# Revit family: xxSink-Single_Bowl-American_Standard-PEKOE-18SB.9332200A.075
name_source: partatom
category: Plumbing Fixtures
revit_build: Autodesk Revit 2014 (Build: 20130308_1515(x64)
units: mm (PartAtom-declared; Revit-internal decimal feet)

## types (1)
- 18SB.9332200A.075
    Assembly Code = D2010410
    Bottom Grid 7434000.075 = Yes
    Bowl Shape = Rectangular Apron Front
    CW Connection = Yes
    CWFU = 1.5
    Cold Water Connection Diameter = 1/2"
    Cold Water Connection Height = 2"
    Cold Water Connection Width = 2"
    Cutout Length = 1 3/8"
    Cutout Width = 33"
    Default Elevation = 0"
    Description = Pekoe® 33 x 22 Single Bowl Apron Front Kitchen Sink 18 Gauge Stainless Steel
    Finish = Stainless Steel-American Standard-075-Satin
    HW Connection = Yes
    HWFU = 1.5
    Height = 9"
    Hot Water Connection Diameter = 1"
    Hot Water Connection Height = 2"
    Hot Water Connection Width = 2"
    Installation Type = Top Mount
    Length = 22"
    Manufacturer = American Standard
    Material = Stainless Steel-American Standard-075-Satin
    Model = 18SB.9332200A.075
    Placement Height = 0"
    Price = Prices may vary. Please consult Manufacturer Representative for most up-to-date price list.
    Product Documentation Link = https://www.americanstandard-us.com
    Product Page URL = https://www.americanstandard-us.com
    Top Mount Installation = Yes
    URL = https://www.americanstandard-us.com
    Undermount Installation = No
    Vent Connection = No
    WFU = 2
    Wall Distance = 1"
    Warranty Information = Limited Lifetime Warranty
    Waste Connection = Yes
    Waste Connection Diameter = 1 1/2"
    Waste Connection Height = 3"
    Waste Fitting 9028000.075 = Yes
    Width = 33"

## geometry (parser evidence)
native form markers: Sweep x1
no freeform markers — native parametric forms only
